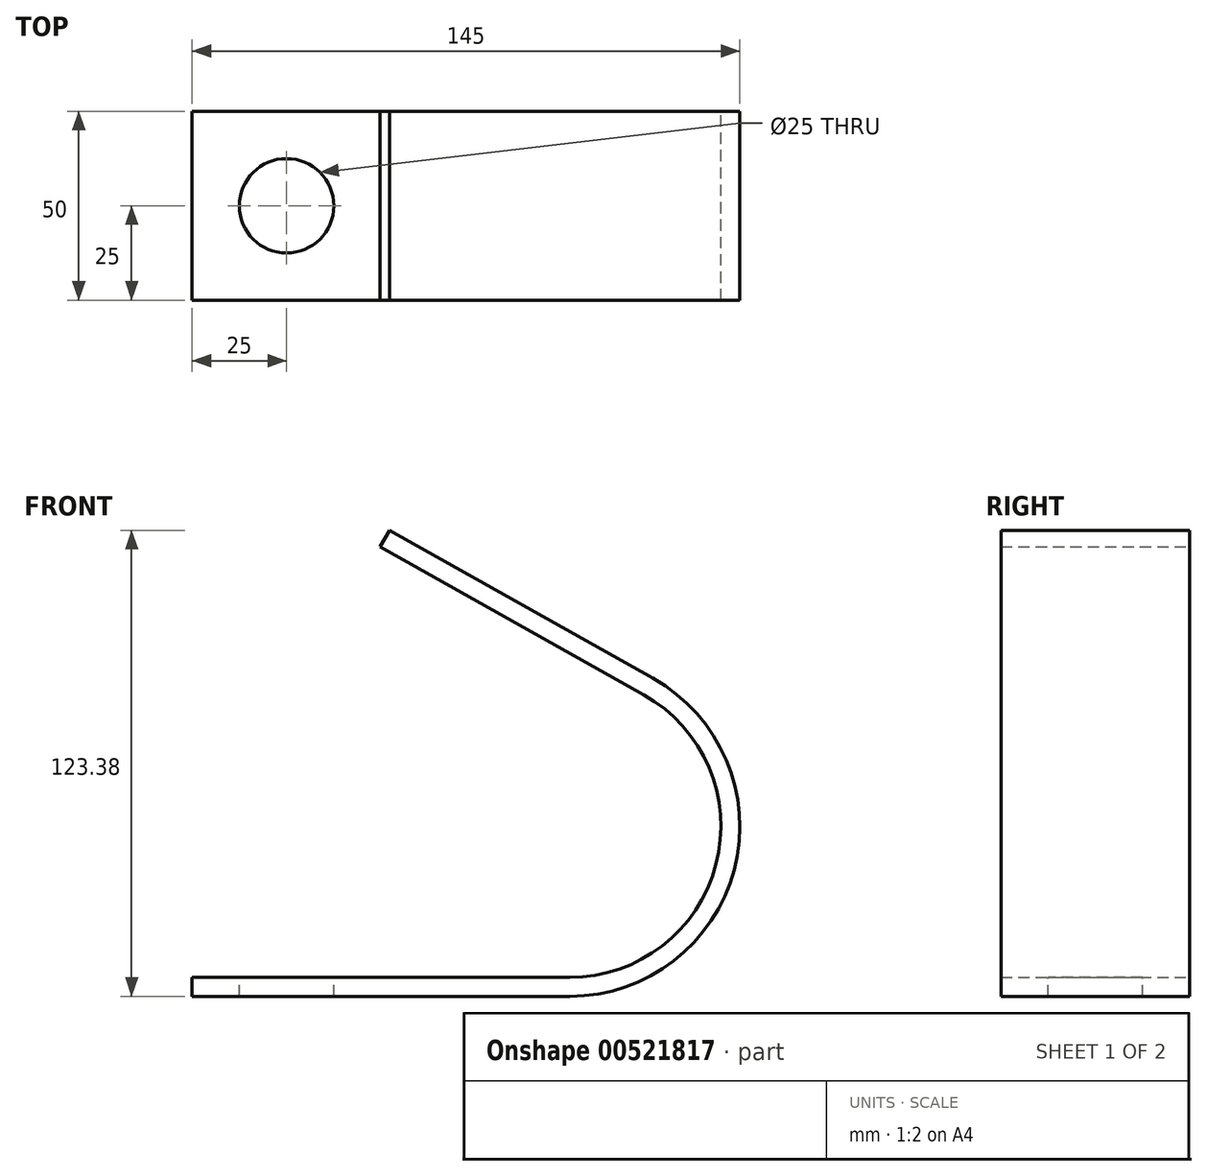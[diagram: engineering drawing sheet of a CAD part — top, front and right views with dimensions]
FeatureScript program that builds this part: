
annotation { "Feature Type Name" : "Feature", "Feature Type Description" : "" }
export const myFeature = defineFeature(function(context is Context, id is Id, definition is map)
    precondition{}
    {
        {
            var Q0;
            Q0=qCreatedBy(makeId("Front.planeOp"),FACE);
            var sketch = newSketch(context, id + "F0", { "sketchPlane" : qUnion([Q0])});
            skLineSegment(sketch, "E0", {"start": v(0, 0) * mm, "end": v(100, 0) * mm});
            skArc(sketch, "E1", {"start": v(100, 0) * mm, "mid": v(138.7, 29.89) * mm, "end": v(119.57, 74.89) * mm});
            skLineSegment(sketch, "E2", {"start": v(119.57, 74.89) * mm, "end": v(49.8, 114.02) * mm});
            skLineSegment(sketch, "E3.0", {"start": v(122.01, 79.25) * mm, "end": v(52.24, 118.38) * mm});
            skArc(sketch, "E3.1", {"start": v(100, -5) * mm, "mid": v(143.54, 28.62) * mm, "end": v(122.01, 79.25) * mm});
            skLineSegment(sketch, "E3.2", {"start": v(0, -5) * mm, "end": v(100, -5) * mm});
            skLineSegment(sketch, "E4", {"start": v(0, 0) * mm, "end": v(0, -5) * mm});
            skLineSegment(sketch, "E5", {"start": v(49.8, 114.02) * mm, "end": v(52.24, 118.38) * mm});
            skSolve(sketch);
        }
        {
            var Q0;
            Q0 = qSketchRegion(id + "F0", true);
            extrude(context, id + "F1", {"entities" : qUnion([Q0]), "depth" : 50 * mm, "offsetDistance" : 25 * mm});
        }
        {
            var Q0;
            Q0=makeQuery(id+"F1.opExtrude","SWEPT_FACE",FACE,{"disambiguationData":[OSD([sQuery(id+"F0.wireOp",EDGE,"E0")])]});
            var sketch = newSketch(context, id + "F2", { "sketchPlane" : qUnion([Q0])});
            skCircle(sketch, "E6", {"center": v(25, -25) * mm, "radius": 12.5 * mm});
            skSolve(sketch);
        }
        {
            var Q0;
            Q0=makeQuery(id+"F2.imprint","IMPRINT",FACE,{"disambiguationData":[TD([[makeQuery(id+"F2.imprint","IMPRINT",EDGE,{"derivedFrom":sQuery(id+"F2.wireOp",EDGE,"E6")}),1.0]])]});
            extrude(context, id + "F3", {"entities" : qUnion([Q0]), "operationType" : NewBodyOperationType.REMOVE, "endBound" : BoundingType.THROUGH_ALL, "oppositeDirection" : true, "depth" : 25 * mm, "offsetDistance" : 25 * mm});
        }
    });
